# Revit family: SE_Trez_TC_4C_3000_With_Pit
name_source: partatom
category: Specialty Equipment
units: mm (PartAtom-declared; Revit-internal decimal feet)

## family parameters
Always vertical = Yes
Cut with Voids When Loaded = Yes
Part Type = Normal
Room Calculation Point = No
Round Connector Dimension = Use Diameter
Shared = No
Work Plane-Based = No

## types (1)
- Platform-2000x5400mm with Door Height 2500mm
    Cabin = Speciality_Equipment_Trez_Cabin : Cabin
    Cabin or Platform = Speciality_Equipment_Trez_Platform : Platform
    Cabin or Platform Back = No
    Clear Depth = 5400 mm  [stored 17.7165 ft]
    Clear Width = 2000 mm  [stored 6.56168 ft]
    Clearance = 370 mm  [stored 1.21391 ft]
    Description = Hydraulic goods only lift with four cylinders.
    Door Clear Height = 2500 mm  [stored 8.2021 ft]
    Door Clear Width = 2000 mm  [stored 6.56168 ft]
    Headroom = 3100 mm
    Manufacturer = TREZ Ltd.
    Model = TC 4C 3000
    Pit Height = 250 mm  [stored 0.82021 ft]
    Platform = Speciality_Equipment_Trez_Platform : Platform
    Platform Material = TREZ_Steel
    Profiles Material = TREZ_Steel
    Rail Height = 7850 mm  [stored 25.7546 ft]
    Real Depth = 5400 mm  [stored 17.7165 ft]
    Real Width = 2000 mm  [stored 6.56168 ft]
    Safe Space = 600 mm
    Safe Working Load = 3000.00 kg
    Shaft = TREZ_Shaft_Space
    Shaft Depth = 5500 mm
    Shaft Width = 2740 mm
    Tower Cladding Material = TREZ_Steel_Cladding
    Travel = 4500 mm
    URL = https://trez.bg

note: [stored X ft] marks values corroborated as IEEE doubles in the binary element streams (Revit-internal decimal feet)

## geometry (parser evidence)
native form markers: Sweep x13
no freeform markers — native parametric forms only
